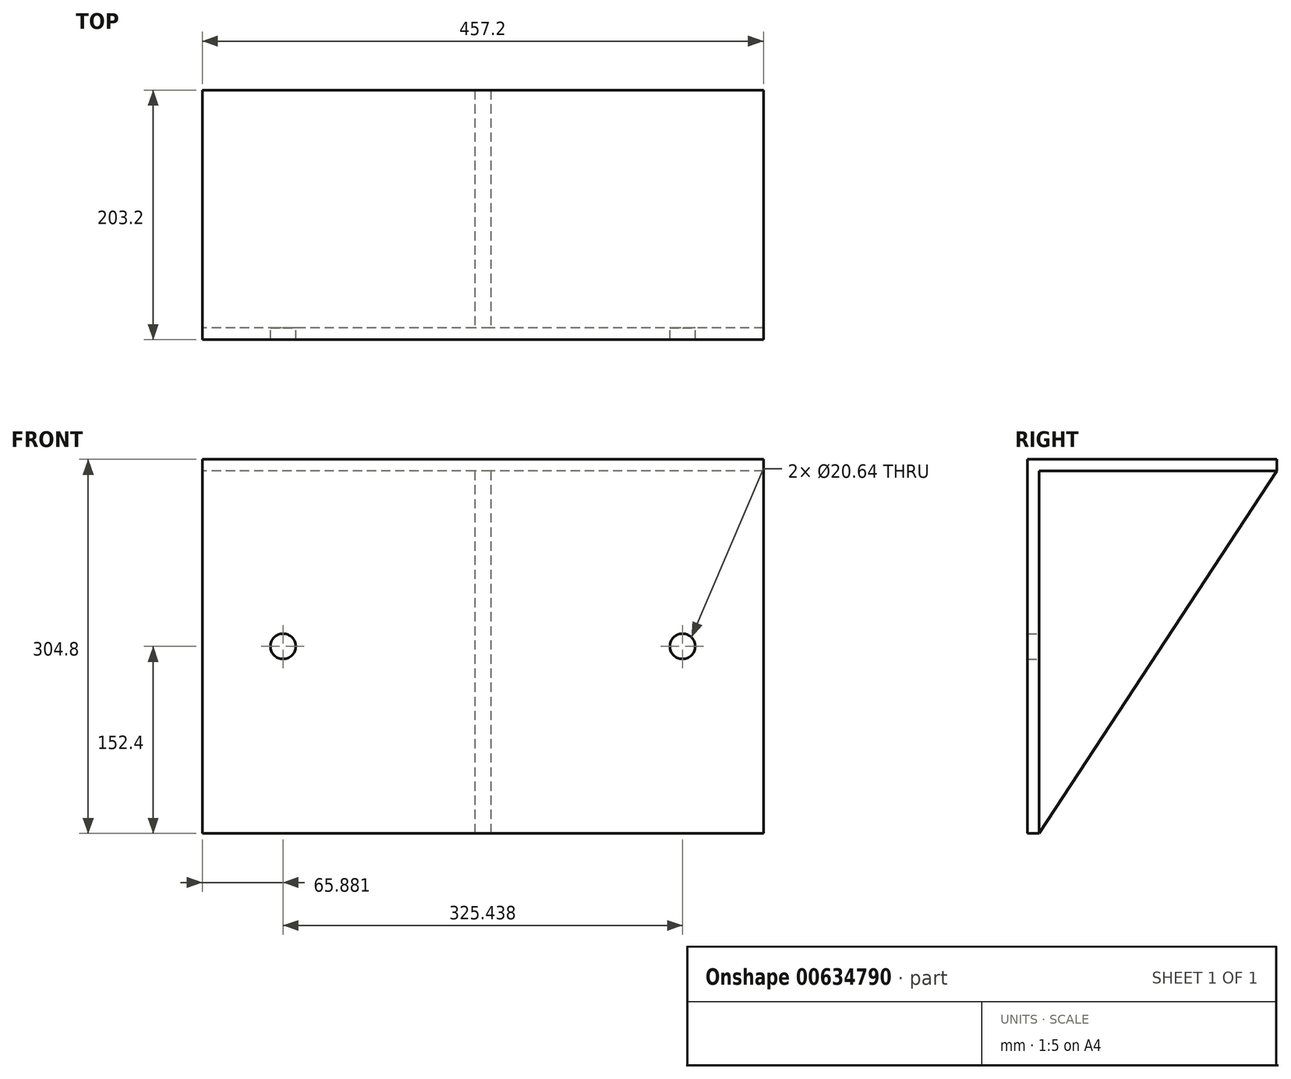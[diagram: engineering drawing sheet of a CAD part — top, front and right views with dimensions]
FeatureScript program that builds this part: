
annotation { "Feature Type Name" : "Feature", "Feature Type Description" : "" }
export const myFeature = defineFeature(function(context is Context, id is Id, definition is map)
    precondition{}
    {
        {
            var Q0;
            Q0=qCreatedBy(makeId("Right.planeOp"),FACE);
            var sketch = newSketch(context, id + "F0", { "sketchPlane" : qUnion([Q0])});
            skLineSegment(sketch, "E0", {"start": v(101.6, 152.4) * mm, "end": v(-101.6, 152.4) * mm});
            skLineSegment(sketch, "E1", {"start": v(-101.6, 152.4) * mm, "end": v(-101.6, -152.4) * mm});
            skLineSegment(sketch, "E2", {"start": v(-101.6, -152.4) * mm, "end": v(-92.07, -152.4) * mm});
            skLineSegment(sketch, "E3", {"start": v(-92.07, -152.4) * mm, "end": v(-92.08, 142.88) * mm});
            skLineSegment(sketch, "E4", {"start": v(-92.08, 142.87) * mm, "end": v(101.6, 142.87) * mm});
            skLineSegment(sketch, "E5", {"start": v(101.6, 142.88) * mm, "end": v(101.6, 152.4) * mm});
            skPoint(sketch, "E6", {"position": v(0, 152.4) * mm});
            skPoint(sketch, "E7", {"position": v(-101.6, 0) * mm});
            skSolve(sketch);
        }
        {
            var Q0;
            Q0 = qSketchRegion(id + "F0", true);
            extrude(context, id + "F1", {"entities" : qUnion([Q0]), "endBound" : BoundingType.SYMMETRIC, "depth" : 457.2 * mm, "offsetDistance" : 25.4 * mm});
        }
        {
            var Q0;
            Q0=qCreatedBy(makeId("Right.planeOp"),FACE);
            var sketch = newSketch(context, id + "F2", { "sketchPlane" : qUnion([Q0])});
            skLineSegment(sketch, "E8", {"start": v(101.6, 142.88) * mm, "end": v(-92.08, 142.87) * mm});
            skLineSegment(sketch, "E9", {"start": v(-92.08, 142.87) * mm, "end": v(-92.08, -152.4) * mm});
            skLineSegment(sketch, "E10", {"start": v(-92.07, -152.4) * mm, "end": v(101.6, 142.88) * mm});
            skSolve(sketch);
        }
        {
            var Q0;
            Q0 = qSketchRegion(id + "F2", true);
            extrude(context, id + "F3", {"entities" : qUnion([Q0]), "operationType" : NewBodyOperationType.ADD, "endBound" : BoundingType.SYMMETRIC, "depth" : 12.7 * mm, "offsetDistance" : 25.4 * mm});
        }
        {
            var Q0;
            {var subQ0=sQuery(id+"F2.wireOp",EDGE,"E10");var subQ3=sQuery(id+"F0.wireOp",EDGE,"E3");Q0=makeQuery(id+"F3.boolean.opBoolean","SPLIT",FACE,{"disambiguationData":[TD([makeQuery(id+"F3.opExtrude","CAP_FACE",FACE,{"disambiguationData":[OSD([sQuery(id+"F2.wireOp",EDGE,"E8"),sQuery(id+"F2.wireOp",EDGE,"E9"),subQ0])],"isStart":false})])],"derivedFrom":makeQuery(id+"F1.opExtrude","SWEPT_FACE",FACE,{"disambiguationData":[OSD([subQ3])]})});}
            var sketch = newSketch(context, id + "F4", { "sketchPlane" : qUnion([Q0])});
            skCircle(sketch, "E11", {"center": v(-162.72, 0) * mm, "radius": 10.32 * mm});
            skCircle(sketch, "E12", {"center": v(162.72, 0) * mm, "radius": 10.32 * mm});
            skLineSegment(sketch, "E13", {"start": v(-162.72, 0) * mm, "end": v(162.72, 0) * mm, "construction": true});
            skSolve(sketch);
        }
        {
            var Q0;
            Q0 = qSketchRegion(id + "F4", true);
            extrude(context, id + "F5", {"entities" : qUnion([Q0]), "operationType" : NewBodyOperationType.REMOVE, "oppositeDirection" : true, "depth" : 25.4 * mm, "offsetDistance" : 25.4 * mm});
        }
    });
